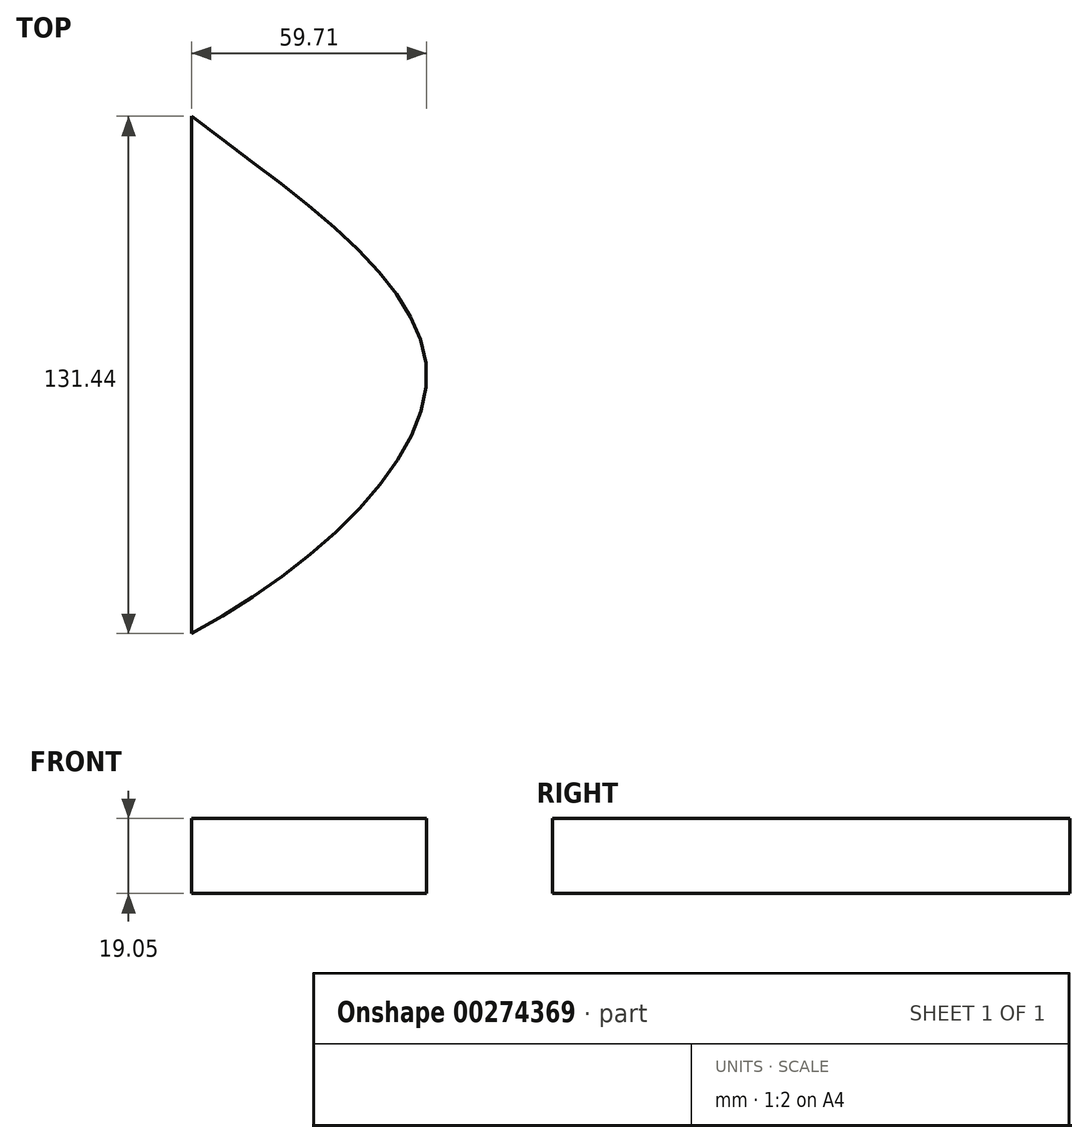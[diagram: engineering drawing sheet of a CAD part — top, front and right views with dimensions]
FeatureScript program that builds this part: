
annotation { "Feature Type Name" : "Feature", "Feature Type Description" : "" }
export const myFeature = defineFeature(function(context is Context, id is Id, definition is map)
    precondition{}
    {
        {
            var Q0;
            Q0=qCreatedBy(makeId("Top.planeOp"),FACE);
            var sketch = newSketch(context, id + "F0", { "sketchPlane" : qUnion([Q0])});
            skFitSpline(sketch, "E0", {"points": [v(0, 65.72) * mm, v(59.71, 0) * mm, v(0, -65.72) * mm], "startDerivative": vector(177.38, -133.42) * mm, "endDerivative": vector(-181.27, -97.82) * mm});
            skLineSegment(sketch, "E1", {"start": v(0, 65.72) * mm, "end": v(0, 0) * mm});
            skLineSegment(sketch, "E2", {"start": v(0, -65.72) * mm, "end": v(0, 0) * mm});
            skSolve(sketch);
        }
        {
            var Q0;
            Q0 = qSketchRegion(id + "F0", true);
            extrude(context, id + "F1", {"entities" : qUnion([Q0]), "depth" : 19.05 * mm});
        }
    });
